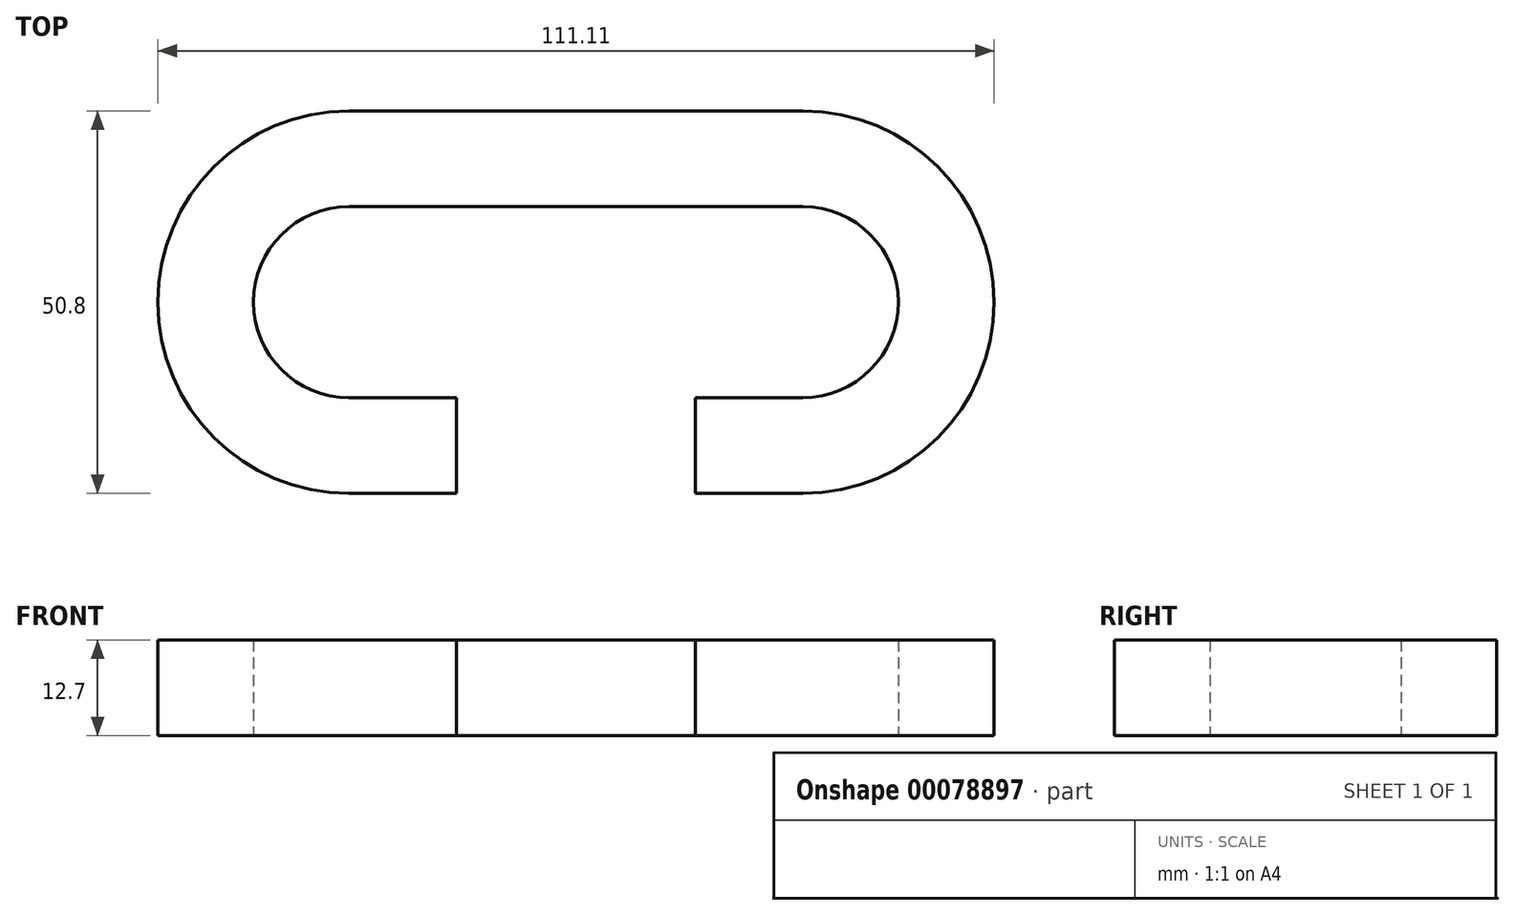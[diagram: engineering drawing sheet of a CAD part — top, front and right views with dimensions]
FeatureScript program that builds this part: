
annotation { "Feature Type Name" : "Feature", "Feature Type Description" : "" }
export const myFeature = defineFeature(function(context is Context, id is Id, definition is map)
    precondition{}
    {
        {
            var Q0;
            Q0=qCreatedBy(makeId("Top.planeOp"),FACE);
            var sketch = newSketch(context, id + "F0", { "sketchPlane" : qUnion([Q0])});
            skLineSegment(sketch, "E0.bottom", {"start": v(15.08, -6.35) * mm, "end": v(-15.08, -6.35) * mm});
            skLineSegment(sketch, "E0.top", {"start": v(15.08, 6.35) * mm, "end": v(-15.08, 6.35) * mm});
            skLineSegment(sketch, "E0.right", {"start": v(-15.08, -6.35) * mm, "end": v(-15.08, 6.35) * mm});
            skPoint(sketch, "E0.middle", {"position": v(0, 0) * mm});
            skArc(sketch, "E1", {"start": v(15.08, -44.45) * mm, "mid": v(40.48, -19.05) * mm, "end": v(15.08, 6.35) * mm});
            skArc(sketch, "E2", {"start": v(15.08, -31.75) * mm, "mid": v(27.78, -19.05) * mm, "end": v(15.08, -6.35) * mm});
            skLineSegment(sketch, "E3.bottom", {"start": v(15.08, -31.75) * mm, "end": v(0.8, -31.75) * mm});
            skLineSegment(sketch, "E3.top", {"start": v(15.08, -44.45) * mm, "end": v(0.8, -44.45) * mm});
            skLineSegment(sketch, "E3.left", {"start": v(15.08, -31.75) * mm, "end": v(15.08, -44.45) * mm});
            skLineSegment(sketch, "E3.right", {"start": v(0.8, -31.75) * mm, "end": v(0.8, -44.45) * mm});
            skSolve(sketch);
        }
        {
            var Q0;
            Q0 = qSketchRegion(id + "F0", true);
            extrude(context, id + "F1", {"entities" : qUnion([Q0]), "depth" : 12.7 * mm});
        }
        {
            var Q0;
            Q0=makeQuery(id+"F1.opExtrude","SWEPT_BODY",BODY,{"disambiguationData":[OSD([sQuery(id+"F0.wireOp",EDGE,"E0.bottom"),sQuery(id+"F0.wireOp",EDGE,"E0.top"),sQuery(id+"F0.wireOp",EDGE,"E0.right"),sQuery(id+"F0.wireOp",EDGE,"E1"),sQuery(id+"F0.wireOp",EDGE,"E2"),sQuery(id+"F0.wireOp",EDGE,"E3.bottom"),sQuery(id+"F0.wireOp",EDGE,"E3.top"),sQuery(id+"F0.wireOp",EDGE,"E3.right")])]});
            var Q1;
            Q1=makeQuery(id+"F1.opExtrude","SWEPT_FACE",FACE,{"disambiguationData":[OSD([sQuery(id+"F0.wireOp",EDGE,"E0.right")])]});
            mirror(context, id + "F2", {"operationType" : NewBodyOperationType.ADD, "entities" : qUnion([Q0]), "mirrorPlane" : qUnion([Q1])});
        }
    });
